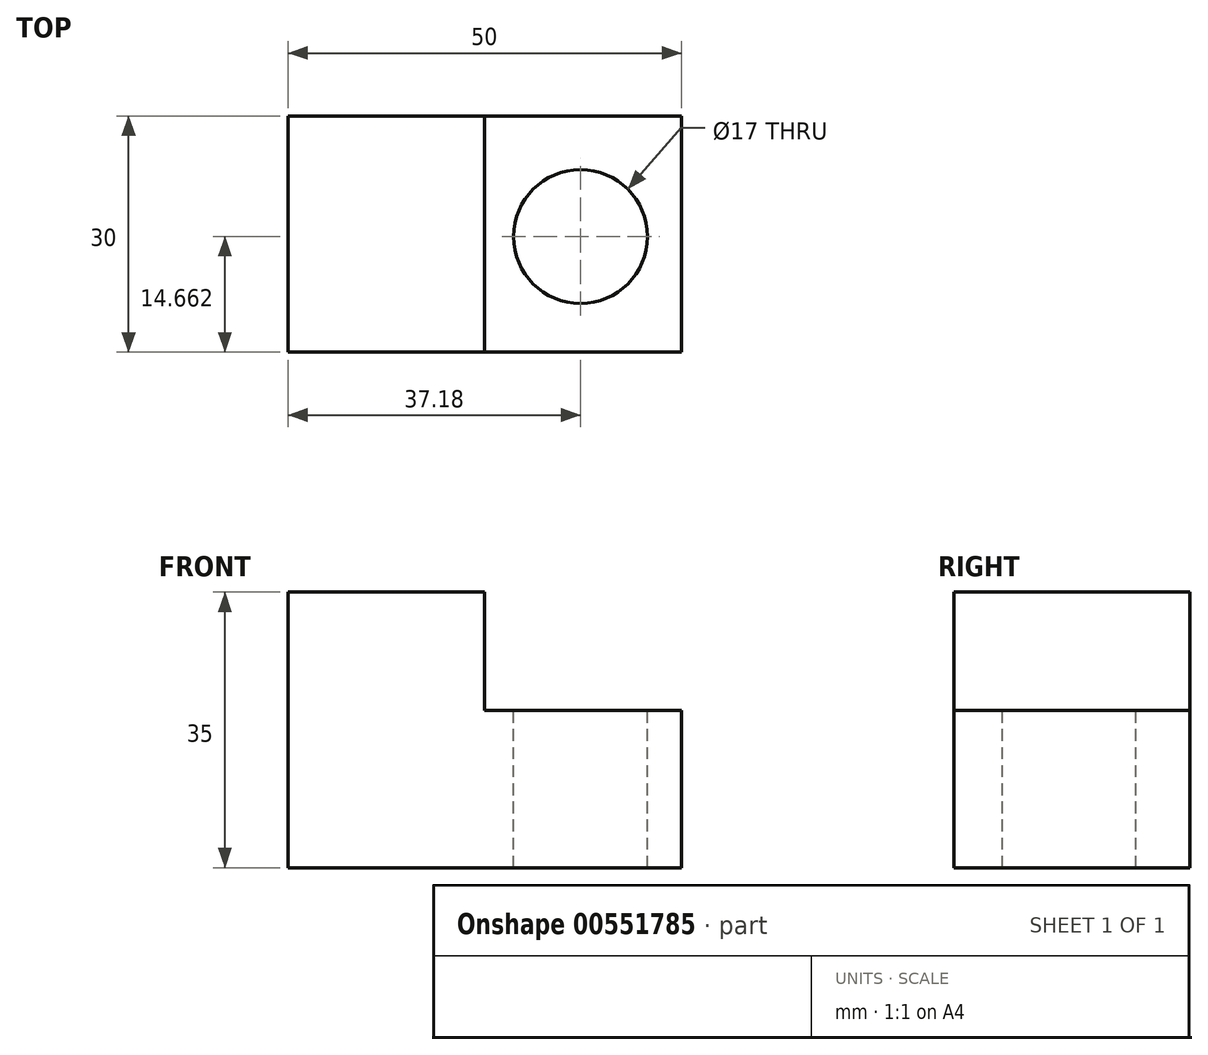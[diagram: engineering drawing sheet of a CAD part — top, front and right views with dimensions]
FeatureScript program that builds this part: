
annotation { "Feature Type Name" : "Feature", "Feature Type Description" : "" }
export const myFeature = defineFeature(function(context is Context, id is Id, definition is map)
    precondition{}
    {
        {
            var Q0;
            Q0=qCreatedBy(makeId("Front.planeOp"),FACE);
            var sketch = newSketch(context, id + "F0", { "sketchPlane" : qUnion([Q0])});
            skLineSegment(sketch, "E0", {"start": v(0, 0) * mm, "end": v(-50, 0) * mm});
            skLineSegment(sketch, "E1", {"start": v(-50, 0) * mm, "end": v(-50, 35) * mm});
            skLineSegment(sketch, "E2", {"start": v(-50, 35) * mm, "end": v(-25, 35) * mm});
            skLineSegment(sketch, "E3", {"start": v(-25, 35) * mm, "end": v(-25, 20) * mm});
            skLineSegment(sketch, "E4", {"start": v(-25, 20) * mm, "end": v(0, 20) * mm});
            skLineSegment(sketch, "E5", {"start": v(0, 20) * mm, "end": v(0, 0) * mm});
            skSolve(sketch);
        }
        {
            var Q0;
            Q0=makeQuery(id+"F0.imprint","IMPRINT",FACE,{"disambiguationData":[TD([[makeQuery(id+"F0.imprint","IMPRINT",EDGE,{"derivedFrom":sQuery(id+"F0.wireOp",EDGE,"E0")}),-1.0]])]});
            extrude(context, id + "F1", {"entities" : qUnion([Q0]), "depth" : 30 * mm, "offsetDistance" : 25 * mm});
        }
        {
            var Q0;
            Q0=makeQuery(id+"F1.opExtrude","SWEPT_FACE",FACE,{"disambiguationData":[OSD([sQuery(id+"F0.wireOp",EDGE,"E4")])]});
            var sketch = newSketch(context, id + "F2", { "sketchPlane" : qUnion([Q0])});
            skCircle(sketch, "E6", {"center": v(-12.82, -15.34) * mm, "radius": 8.5 * mm});
            skSolve(sketch);
        }
        {
            var Q0;
            Q0=qSketchRegion(id+"F2",true);
            extrude(context, id + "F3", {"entities" : qUnion([Q0]), "operationType" : NewBodyOperationType.REMOVE, "oppositeDirection" : true, "depth" : 25 * mm, "offsetDistance" : 25 * mm});
        }
    });
